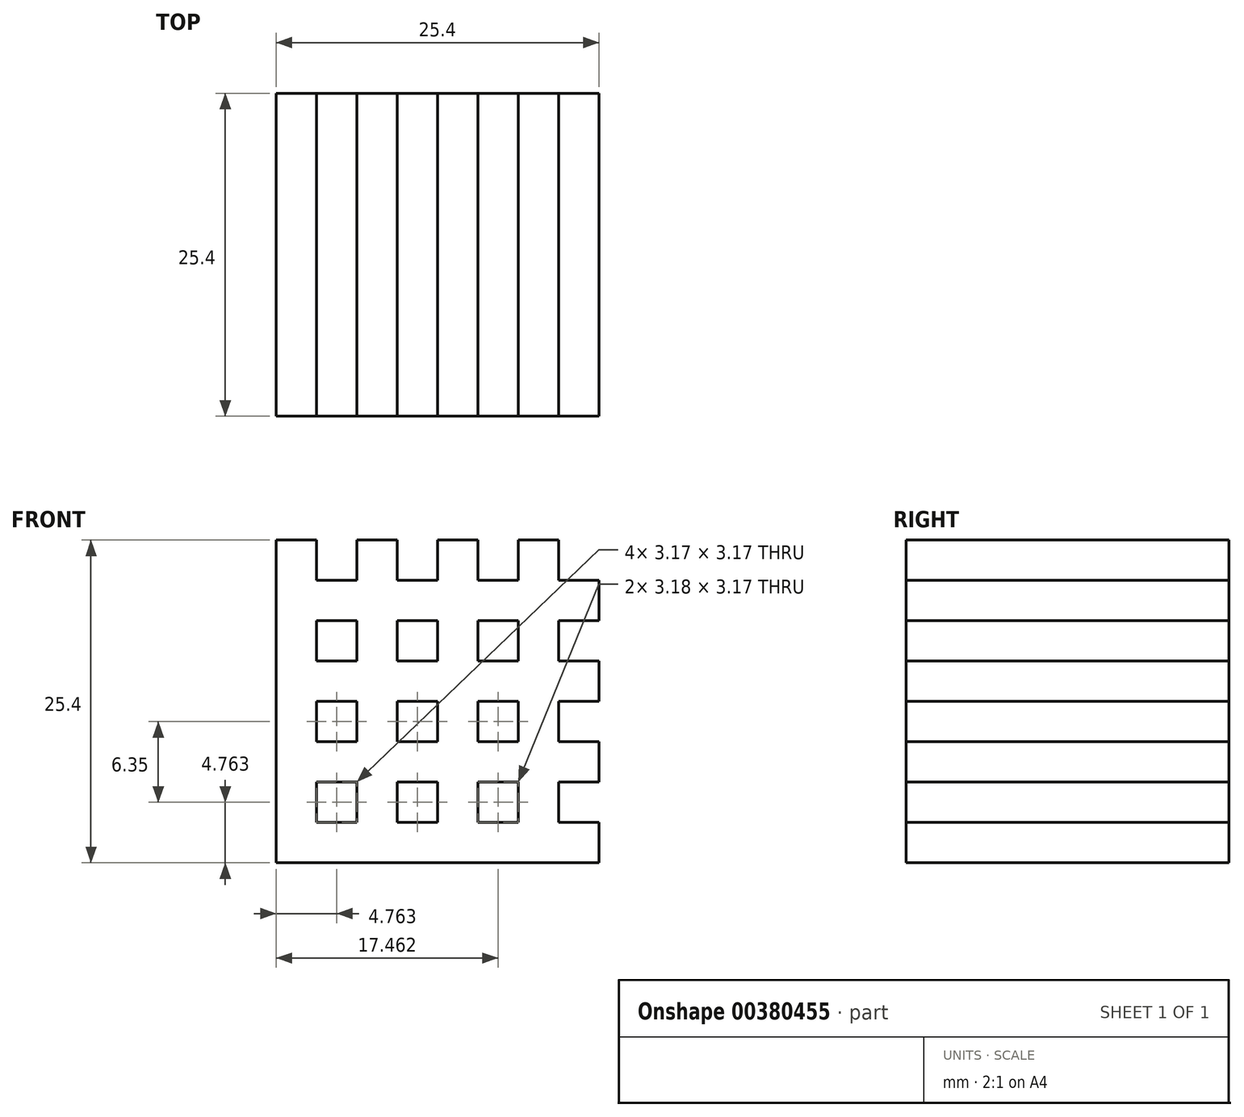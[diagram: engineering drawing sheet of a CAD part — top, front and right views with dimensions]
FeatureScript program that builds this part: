
annotation { "Feature Type Name" : "Feature", "Feature Type Description" : "" }
export const myFeature = defineFeature(function(context is Context, id is Id, definition is map)
    precondition{}
    {
        {
            var Q0;
            Q0=qCreatedBy(makeId("Top.planeOp"),FACE);
            var sketch = newSketch(context, id + "F0", { "sketchPlane" : qUnion([Q0])});
            skLineSegment(sketch, "E0", {"start": v(0, 0) * mm, "end": v(0, 25.4) * mm});
            skLineSegment(sketch, "E1", {"start": v(0, 25.4) * mm, "end": v(25.4, 25.4) * mm});
            skLineSegment(sketch, "E2", {"start": v(25.4, 25.4) * mm, "end": v(25.4, 0) * mm});
            skLineSegment(sketch, "E3", {"start": v(25.4, 0) * mm, "end": v(0, 0) * mm});
            skLineSegment(sketch, "E4", {"start": v(3.18, 25.4) * mm, "end": v(3.18, 0) * mm});
            skLineSegment(sketch, "E5", {"start": v(6.35, 25.4) * mm, "end": v(6.35, 0) * mm});
            skLineSegment(sketch, "E6", {"start": v(6.35, 0) * mm, "end": v(12.7, 0) * mm});
            skLineSegment(sketch, "E7", {"start": v(12.7, 0) * mm, "end": v(12.7, 25.4) * mm});
            skLineSegment(sketch, "E8", {"start": v(12.7, 25.4) * mm, "end": v(15.88, 25.4) * mm});
            skLineSegment(sketch, "E9", {"start": v(15.88, 25.4) * mm, "end": v(15.88, 0) * mm});
            skLineSegment(sketch, "E10", {"start": v(15.88, 0) * mm, "end": v(19.05, 0) * mm});
            skLineSegment(sketch, "E11", {"start": v(19.05, 0) * mm, "end": v(19.05, 25.4) * mm});
            skLineSegment(sketch, "E12", {"start": v(19.05, 25.4) * mm, "end": v(25.4, 25.4) * mm});
            skLineSegment(sketch, "E13", {"start": v(9.53, 25.4) * mm, "end": v(9.53, 0) * mm});
            skLineSegment(sketch, "E14", {"start": v(22.23, 25.4) * mm, "end": v(22.23, 0) * mm});
            skSolve(sketch);
        }
        {
            var Q0;
            {var subQ0=sQuery(id+"F0.wireOp",EDGE,"E0");Q0=makeQuery(id+"F0.imprint","IMPRINT",FACE,{"disambiguationData":[TD([[makeQuery(id+"F0.imprint","IMPRINT",EDGE,{"derivedFrom":subQ0}),-1.0]])]});}
            var Q1;
            {var subQ0=sQuery(id+"F0.wireOp",EDGE,"E5");Q1=makeQuery(id+"F0.imprint","IMPRINT",FACE,{"disambiguationData":[TD([[makeQuery(id+"F0.imprint","IMPRINT",EDGE,{"derivedFrom":subQ0}),1.0]])]});}
            var Q2;
            {var subQ0=sQuery(id+"F0.wireOp",EDGE,"E7");Q2=makeQuery(id+"F0.imprint","IMPRINT",FACE,{"disambiguationData":[TD([[makeQuery(id+"F0.imprint","IMPRINT",EDGE,{"derivedFrom":subQ0}),-1.0]])]});}
            var Q3;
            {var subQ0=sQuery(id+"F0.wireOp",EDGE,"E11");Q3=makeQuery(id+"F0.imprint","IMPRINT",FACE,{"disambiguationData":[TD([[makeQuery(id+"F0.imprint","IMPRINT",EDGE,{"derivedFrom":subQ0}),-1.0]])]});}
            extrude(context, id + "F1", {"entities" : qUnion([Q0, Q1, Q2, Q3]), "depth" : 25.4 * mm});
        }
        {
            var Q0;
            Q0=qCreatedBy(makeId("Front.planeOp"),FACE);
            var sketch = newSketch(context, id + "F2", { "sketchPlane" : qUnion([Q0])});
            skLineSegment(sketch, "E15", {"start": v(0, 25.4) * mm, "end": v(25.4, 25.4) * mm});
            skLineSegment(sketch, "E16", {"start": v(25.4, 25.4) * mm, "end": v(25.4, 0) * mm});
            skLineSegment(sketch, "E17", {"start": v(25.4, 0) * mm, "end": v(0, 0) * mm});
            skLineSegment(sketch, "E18", {"start": v(0, 0) * mm, "end": v(0, 25.4) * mm});
            skLineSegment(sketch, "E19", {"start": v(0, 22.23) * mm, "end": v(25.4, 22.23) * mm});
            skLineSegment(sketch, "E20", {"start": v(25.4, 22.23) * mm, "end": v(25.4, 19.05) * mm});
            skLineSegment(sketch, "E21", {"start": v(25.4, 19.05) * mm, "end": v(0, 19.05) * mm});
            skLineSegment(sketch, "E22", {"start": v(0, 19.05) * mm, "end": v(0, 12.7) * mm});
            skLineSegment(sketch, "E23", {"start": v(0, 12.7) * mm, "end": v(25.4, 12.7) * mm});
            skLineSegment(sketch, "E24", {"start": v(25.4, 12.7) * mm, "end": v(25.4, 15.88) * mm});
            skLineSegment(sketch, "E25", {"start": v(25.4, 15.88) * mm, "end": v(0, 15.88) * mm});
            skLineSegment(sketch, "E26", {"start": v(0, 15.88) * mm, "end": v(0, 9.52) * mm});
            skLineSegment(sketch, "E27", {"start": v(0, 9.52) * mm, "end": v(25.4, 9.53) * mm});
            skLineSegment(sketch, "E28", {"start": v(25.4, 9.53) * mm, "end": v(25.4, 3.18) * mm});
            skLineSegment(sketch, "E29", {"start": v(25.4, 3.18) * mm, "end": v(0, 3.17) * mm});
            skLineSegment(sketch, "E30", {"start": v(0, 6.35) * mm, "end": v(25.4, 6.35) * mm});
            skSolve(sketch);
        }
        {
            var Q0;
            {var subQ0=sQuery(id+"F2.wireOp",EDGE,"E17");Q0=makeQuery(id+"F2.imprint","IMPRINT",FACE,{"disambiguationData":[TD([[makeQuery(id+"F2.imprint","IMPRINT",EDGE,{"derivedFrom":subQ0}),-1.0]])]});}
            var Q1;
            {var subQ0=sQuery(id+"F2.wireOp",EDGE,"E27");Q1=makeQuery(id+"F2.imprint","IMPRINT",FACE,{"disambiguationData":[TD([[makeQuery(id+"F2.imprint","IMPRINT",EDGE,{"derivedFrom":subQ0}),-1.0]])]});}
            var Q2;
            {var subQ0=sQuery(id+"F2.wireOp",EDGE,"E23");Q2=makeQuery(id+"F2.imprint","IMPRINT",FACE,{"disambiguationData":[TD([[makeQuery(id+"F2.imprint","IMPRINT",EDGE,{"derivedFrom":subQ0}),1.0]])]});}
            var Q3;
            {var subQ0=sQuery(id+"F2.wireOp",EDGE,"E19");Q3=makeQuery(id+"F2.imprint","IMPRINT",FACE,{"disambiguationData":[TD([[makeQuery(id+"F2.imprint","IMPRINT",EDGE,{"derivedFrom":subQ0}),-1.0]])]});}
            extrude(context, id + "F3", {"entities" : qUnion([Q0, Q1, Q2, Q3]), "operationType" : NewBodyOperationType.ADD, "oppositeDirection" : true, "depth" : 25.4 * mm});
        }
    });
